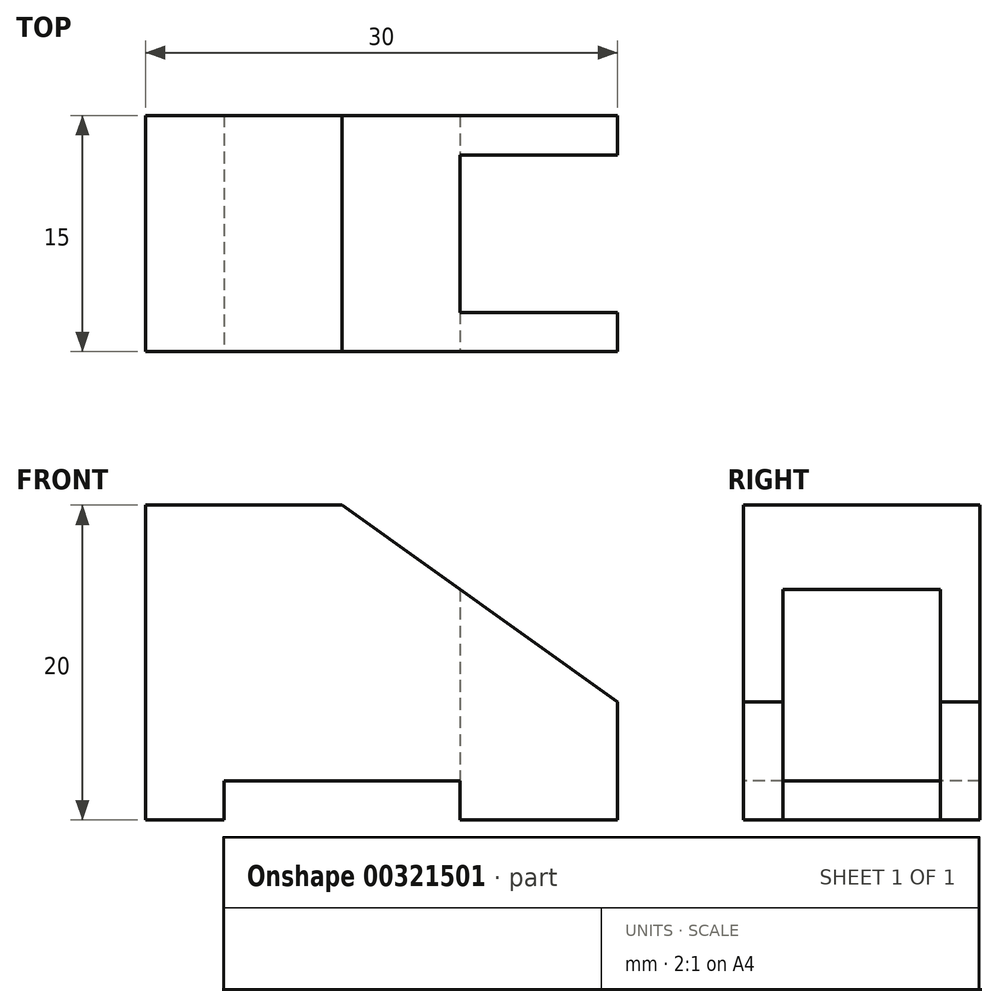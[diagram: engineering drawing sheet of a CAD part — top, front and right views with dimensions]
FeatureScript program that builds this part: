
annotation { "Feature Type Name" : "Feature", "Feature Type Description" : "" }
export const myFeature = defineFeature(function(context is Context, id is Id, definition is map)
    precondition{}
    {
        {
            var Q0;
            Q0=qCreatedBy(makeId("Front.planeOp"),FACE);
            var sketch = newSketch(context, id + "F0", { "sketchPlane" : qUnion([Q0])});
            skLineSegment(sketch, "E0", {"start": v(0, 0) * mm, "end": v(0, 20) * mm});
            skLineSegment(sketch, "E1", {"start": v(0, 20) * mm, "end": v(30, 20) * mm});
            skLineSegment(sketch, "E2", {"start": v(30, 20) * mm, "end": v(30, 0) * mm});
            skLineSegment(sketch, "E3", {"start": v(30, 0) * mm, "end": v(0, 0) * mm});
            skSolve(sketch);
        }
        {
            var Q0;
            Q0=makeQuery(id+"F0.imprint","IMPRINT",FACE,{"disambiguationData":[TD([[makeQuery(id+"F0.imprint","IMPRINT",EDGE,{"derivedFrom":sQuery(id+"F0.wireOp",EDGE,"E0")}),-1.0]])]});
            extrude(context, id + "F1", {"entities" : qUnion([Q0]), "endBound" : BoundingType.SYMMETRIC, "depth" : 15 * mm});
        }
        {
            var Q0;
            Q0=makeQuery(id+"F1.opExtrude","CAP_FACE",FACE,{"disambiguationData":[OSD([sQuery(id+"F0.wireOp",EDGE,"E0"),sQuery(id+"F0.wireOp",EDGE,"E1"),sQuery(id+"F0.wireOp",EDGE,"E2"),sQuery(id+"F0.wireOp",EDGE,"E3")])],"isStart":false});
            var sketch = newSketch(context, id + "F2", { "sketchPlane" : qUnion([Q0])});
            skLineSegment(sketch, "E4", {"start": v(0, 20) * mm, "end": v(0, 0) * mm});
            skLineSegment(sketch, "E5", {"start": v(0, 0) * mm, "end": v(5, 0) * mm});
            skLineSegment(sketch, "E6", {"start": v(5, 0) * mm, "end": v(5, 2.5) * mm});
            skLineSegment(sketch, "E7", {"start": v(5, 2.5) * mm, "end": v(20, 2.5) * mm});
            skLineSegment(sketch, "E8", {"start": v(20, 2.5) * mm, "end": v(20, 0) * mm});
            skLineSegment(sketch, "E9", {"start": v(20, 0) * mm, "end": v(30, 0) * mm});
            skLineSegment(sketch, "E10", {"start": v(30, 0) * mm, "end": v(30, 7.5) * mm});
            skLineSegment(sketch, "E11", {"start": v(0, 20) * mm, "end": v(12.5, 20) * mm});
            skLineSegment(sketch, "E12", {"start": v(12.5, 20) * mm, "end": v(30, 7.5) * mm});
            skSolve(sketch);
        }
        {
            var Q0;
            {var subQ0=sQuery(id+"F2.wireOp",EDGE,"E12");Q0=makeQuery(id+"F2.imprint","IMPRINT",FACE,{"disambiguationData":[TD([[makeQuery(id+"F2.imprint","IMPRINT",EDGE,{"derivedFrom":subQ0}),1.0]])]});}
            var Q1;
            {var subQ0=sQuery(id+"F2.wireOp",EDGE,"E6");Q1=makeQuery(id+"F2.imprint","IMPRINT",FACE,{"disambiguationData":[TD([[makeQuery(id+"F2.imprint","IMPRINT",EDGE,{"derivedFrom":subQ0}),-1.0]])]});}
            extrude(context, id + "F3", {"entities" : qUnion([Q0, Q1]), "operationType" : NewBodyOperationType.REMOVE, "endBound" : BoundingType.THROUGH_ALL, "oppositeDirection" : true, "depth" : 25 * mm});
        }
        {
            var Q0;
            {var subQ0=sQuery(id+"F0.wireOp",EDGE,"E3");var subQ1=sQuery(id+"F0.wireOp",EDGE,"E2");Q0=makeQuery(id+"F3.boolean.opBoolean","SPLIT",FACE,{"disambiguationData":[TD([makeQuery(id+"F1.opExtrude","SWEPT_FACE",FACE,{"disambiguationData":[OSD([subQ1])]})])],"derivedFrom":makeQuery(id+"F1.opExtrude","SWEPT_FACE",FACE,{"disambiguationData":[OSD([subQ0])]})});}
            var sketch = newSketch(context, id + "F4", { "sketchPlane" : qUnion([Q0])});
            skLineSegment(sketch, "E13", {"start": v(30, 7.5) * mm, "end": v(30, 5) * mm});
            skLineSegment(sketch, "E14", {"start": v(30, 5) * mm, "end": v(20, 5) * mm});
            skLineSegment(sketch, "E15", {"start": v(30, -7.5) * mm, "end": v(30, -5) * mm});
            skLineSegment(sketch, "E16", {"start": v(30, -5) * mm, "end": v(20, -5) * mm});
            skLineSegment(sketch, "E17", {"start": v(20, -5) * mm, "end": v(20, 5) * mm});
            skSolve(sketch);
        }
        {
            var Q0;
            {var subQ0=sQuery(id+"F4.wireOp",EDGE,"E14");Q0=makeQuery(id+"F4.imprint","IMPRINT",FACE,{"disambiguationData":[TD([[makeQuery(id+"F4.imprint","IMPRINT",EDGE,{"derivedFrom":subQ0}),1.0]])]});}
            extrude(context, id + "F5", {"entities" : qUnion([Q0]), "operationType" : NewBodyOperationType.REMOVE, "endBound" : BoundingType.THROUGH_ALL, "oppositeDirection" : true, "depth" : 25 * mm});
        }
    });
